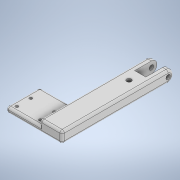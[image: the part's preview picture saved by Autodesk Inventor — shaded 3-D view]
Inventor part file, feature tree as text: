
AUTODESK INVENTOR PART (.ipt)
format: ipt  version: 2020 (Build 240168000, 168)  size: 203,264 bytes
history: native  units: mm
features: fillet x5, extrude x4, sketch x3, projected_geometry x2
ambient origin geometry x8: Origin, YZ Plane, XZ Plane, XY Plane, X Axis, Y Axis, Z Axis, Center Point
bodies: Solid1 (feature_tree)
feature tree (14):
  sketch  "Sketch1"  dims[d0=20.0mm d1=10.0mm]
  extrude  "Extrusion1"  Depth=10.0mm
  extrude  "Extrusion2"  Depth=20.0mm
  fillet  "Fillet1"  Radius=5.0mm
  extrude  "Extrusion3"  Depth=10.0mm TaperAngle=0.0deg
  fillet  "Fillet3"  Radius=30.0mm
  fillet  "Fillet4"  Radius=30.0mm
  fillet  "Fillet5"  Radius=2.5mm
  extrude  "Extrusion4"  Depth=2.0mm
  fillet  "Fillet6"  Radius=5.0mm
  sketch  "Sketch2"  dims[d2=100.0mm d3=20.0mm d4=5.0mm]
  projected_geometry  "Projected Loop1"
  sketch  "Sketch3"  dims[d5=5.0mm d6=10.0mm d7=0.0mm d8=30.0mm d9=30.0mm d10=2.5mm d11=4.5mm d12=5.0mm d13=20.0mm d15=21.0mm d16=20.0mm d18=12.5mm d21=5.0mm d22=0.0mm d23=5.0mm d24=4.0mm d25=81.0mm d26=0.0mm d28=2.0mm d29=2.0mm d30=2.0mm d31=4.2mm d32=10.0mm d33=81.0mm d34=0.0mm d35=2.0mm]
  projected_geometry  "Projected Loop2"
